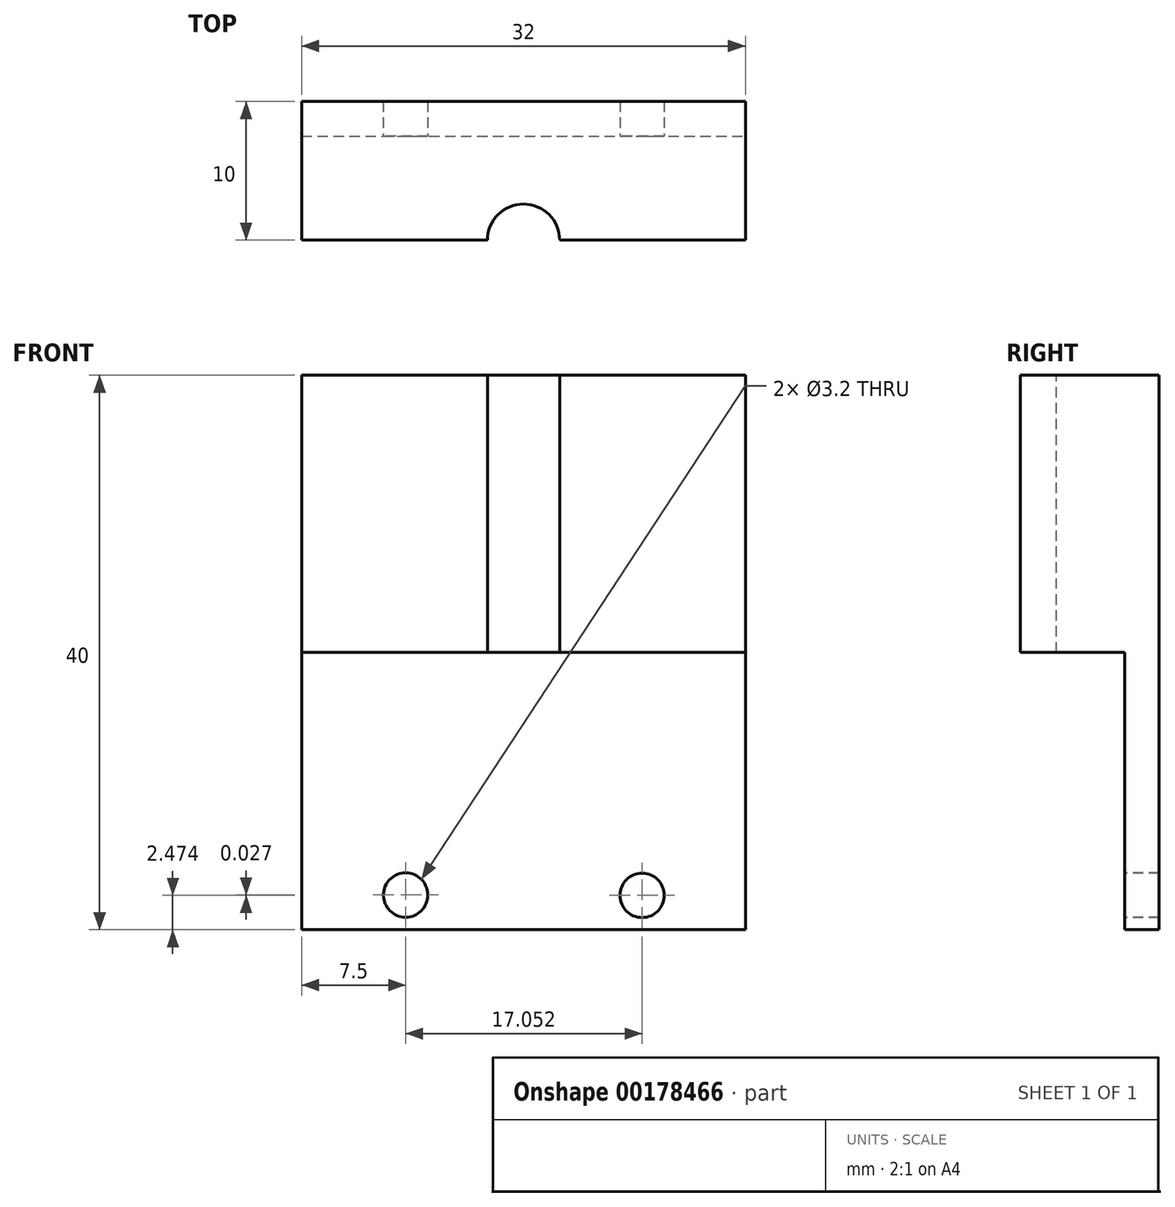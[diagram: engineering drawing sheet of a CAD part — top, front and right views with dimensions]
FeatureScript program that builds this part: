
annotation { "Feature Type Name" : "Feature", "Feature Type Description" : "" }
export const myFeature = defineFeature(function(context is Context, id is Id, definition is map)
    precondition{}
    {
        {
            var Q0;
            Q0=qCreatedBy(makeId("Front.planeOp"),FACE);
            var sketch = newSketch(context, id + "F0", { "sketchPlane" : qUnion([Q0])});
            skLineSegment(sketch, "E0.bottom", {"start": v(-32.53, -35.33) * mm, "end": v(-0.53, -35.33) * mm});
            skLineSegment(sketch, "E0.top", {"start": v(-32.53, 4.67) * mm, "end": v(-0.53, 4.67) * mm});
            skLineSegment(sketch, "E0.left", {"start": v(-32.53, -35.33) * mm, "end": v(-32.53, 4.67) * mm});
            skLineSegment(sketch, "E0.right", {"start": v(-0.53, -35.33) * mm, "end": v(-0.53, 4.67) * mm});
            skSolve(sketch);
        }
        {
            var Q0;
            Q0=makeQuery(id+"F0.imprint","IMPRINT",FACE,{"disambiguationData":[TD([[makeQuery(id+"F0.imprint","IMPRINT",EDGE,{"derivedFrom":sQuery(id+"F0.wireOp",EDGE,"E0.bottom")}),1.0]])]});
            extrude(context, id + "F1", {"entities" : qUnion([Q0]), "depth" : 2.5 * mm});
        }
        {
            var Q0;
            Q0=makeQuery(id+"F1.opExtrude","CAP_FACE",FACE,{"disambiguationData":[OSD([sQuery(id+"F0.wireOp",EDGE,"E0.bottom"),sQuery(id+"F0.wireOp",EDGE,"E0.top"),sQuery(id+"F0.wireOp",EDGE,"E0.left"),sQuery(id+"F0.wireOp",EDGE,"E0.right")])],"isStart":false});
            var sketch = newSketch(context, id + "F2", { "sketchPlane" : qUnion([Q0])});
            skLineSegment(sketch, "E1.bottom", {"start": v(-32.53, -35.33) * mm, "end": v(-0.53, -35.33) * mm});
            skLineSegment(sketch, "E1.top", {"start": v(-32.53, -15.33) * mm, "end": v(-0.53, -15.33) * mm});
            skLineSegment(sketch, "E1.left", {"start": v(-32.53, -35.33) * mm, "end": v(-32.53, -15.33) * mm});
            skLineSegment(sketch, "E1.right", {"start": v(-0.53, -35.33) * mm, "end": v(-0.53, -15.33) * mm});
            skSolve(sketch);
        }
        {
            var Q0;
            {var subQ0=sQuery(id+"F2.wireOp",EDGE,"E1.top");Q0=makeQuery(id+"F2.imprint","IMPRINT",FACE,{"disambiguationData":[TD([[makeQuery(id+"F2.imprint","IMPRINT",EDGE,{"derivedFrom":subQ0}),1.0]])]});}
            extrude(context, id + "F3", {"entities" : qUnion([Q0]), "operationType" : NewBodyOperationType.ADD, "depth" : 7.5 * mm});
        }
        {
            var Q0;
            Q0=makeQuery(id+"F1.opExtrude","CAP_FACE",FACE,{"disambiguationData":[OSD([sQuery(id+"F0.wireOp",EDGE,"E0.bottom"),sQuery(id+"F0.wireOp",EDGE,"E0.top"),sQuery(id+"F0.wireOp",EDGE,"E0.left"),sQuery(id+"F0.wireOp",EDGE,"E0.right")])],"isStart":false});
            var sketch = newSketch(context, id + "F4", { "sketchPlane" : qUnion([Q0])});
            skLineSegment(sketch, "E2", {"start": v(-32.53, -35.33) * mm, "end": v(-32.53, -32.83) * mm, "construction": true});
            skLineSegment(sketch, "E3", {"start": v(-32.53, -32.83) * mm, "end": v(-0.53, -32.83) * mm, "construction": true});
            skLineSegment(sketch, "E4", {"start": v(-32.53, -32.83) * mm, "end": v(-25.03, -32.83) * mm, "construction": true});
            skCircle(sketch, "E5", {"center": v(-25.03, -32.83) * mm, "radius": 1.6 * mm});
            skLineSegment(sketch, "E6", {"start": v(-0.53, -32.83) * mm, "end": v(-8.03, -32.83) * mm});
            skCircle(sketch, "E7", {"center": v(-7.98, -32.86) * mm, "radius": 1.6 * mm});
            skSolve(sketch);
        }
        {
            var Q0;
            Q0=makeQuery(id+"F4.imprint","IMPRINT",FACE,{"disambiguationData":[TD([[makeQuery(id+"F4.imprint","IMPRINT",EDGE,{"derivedFrom":sQuery(id+"F4.wireOp",EDGE,"E5")}),1.0]])]});
            var Q1;
            Q1=makeQuery(id+"F4.imprint","IMPRINT",FACE,{"disambiguationData":[TD([[makeQuery(id+"F4.imprint","IMPRINT",EDGE,{"derivedFrom":sQuery(id+"F4.wireOp",EDGE,"E7")}),1.0]])]});
            var Q2;
            Q2=sQuery(id+"F4.wireOp",EDGE,"E5");
            var Q3;
            Q3=sQuery(id+"F4.wireOp",EDGE,"E7");
            extrude(context, id + "F5", {"entities" : qUnion([Q0, Q1]), "operationType" : NewBodyOperationType.REMOVE, "surfaceEntities" : qUnion([Q2, Q3]), "endBound" : BoundingType.THROUGH_ALL, "oppositeDirection" : true, "depth" : 25 * mm});
        }
        {
            var Q0;
            {var subQ0=sQuery(id+"F0.wireOp",EDGE,"E0.top");Q0=makeQuery(id+"F3.boolean.opBoolean","MERGE",FACE,{"derivedFrom":[makeQuery(id+"F1.opExtrude","SWEPT_FACE",FACE,{"disambiguationData":[OSD([subQ0])]}),makeQuery(id+"F3.opExtrude","SWEPT_FACE",FACE,{"disambiguationData":[OSD([subQ0])]})]});}
            var sketch = newSketch(context, id + "F6", { "sketchPlane" : qUnion([Q0])});
            skCircle(sketch, "E8", {"center": v(-16.53, -10) * mm, "radius": 2.6 * mm});
            skSolve(sketch);
        }
        {
            var Q0;
            Q0 = qSketchRegion(id + "F6", true);
            var Q1;
            Q1=makeQuery(id+"F3.opExtrude","SWEPT_FACE",FACE,{"disambiguationData":[OSD([sQuery(id+"F2.wireOp",EDGE,"E1.top")])]});
            extrude(context, id + "F7", {"entities" : qUnion([Q0]), "operationType" : NewBodyOperationType.REMOVE, "endBound" : BoundingType.UP_TO_SURFACE, "oppositeDirection" : true, "endBoundEntityFace" : qUnion([Q1]), "depth" : 25 * mm});
        }
    });
